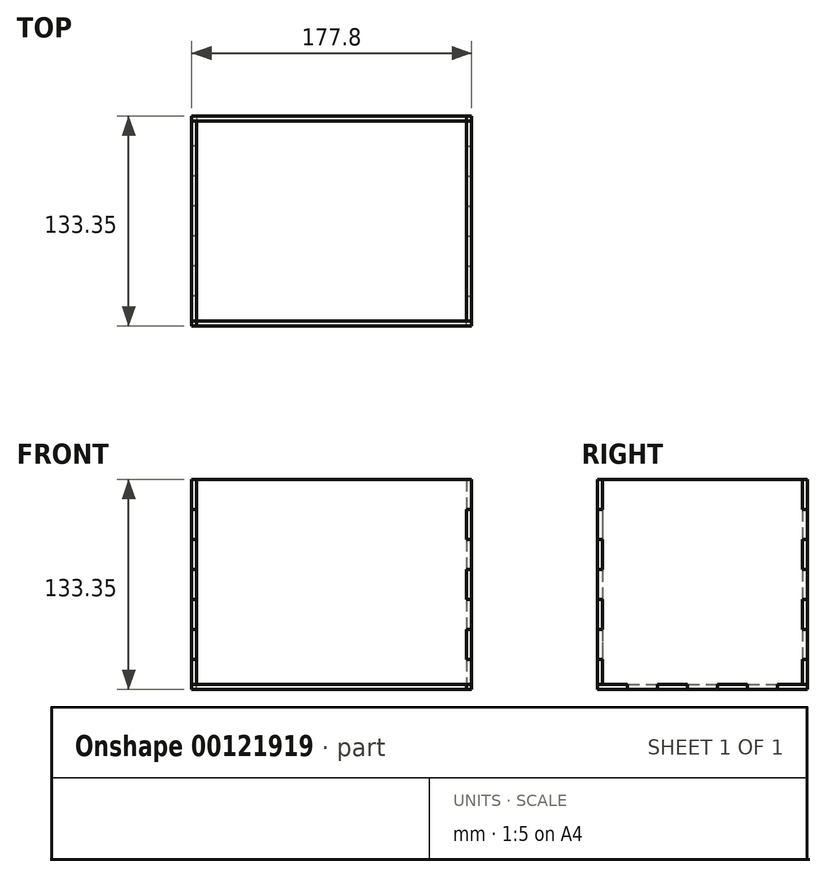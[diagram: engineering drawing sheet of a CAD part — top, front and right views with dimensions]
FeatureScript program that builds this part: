
annotation { "Feature Type Name" : "Feature", "Feature Type Description" : "" }
export const myFeature = defineFeature(function(context is Context, id is Id, definition is map)
    precondition{}
    {
        {
            var Q0;
            Q0=qCreatedBy(makeId("Top.planeOp"),FACE);
            var sketch = newSketch(context, id + "F0", { "sketchPlane" : qUnion([Q0])});
            skLineSegment(sketch, "E0.bottom", {"start": v(-88.9, 66.67) * mm, "end": v(88.9, 66.67) * mm});
            skLineSegment(sketch, "E0.top", {"start": v(-88.9, -66.68) * mm, "end": v(88.9, -66.68) * mm});
            skLineSegment(sketch, "E0.left", {"start": v(-88.9, 66.67) * mm, "end": v(-88.9, -66.68) * mm});
            skLineSegment(sketch, "E0.right", {"start": v(88.9, 66.68) * mm, "end": v(88.9, -66.68) * mm});
            skPoint(sketch, "E0.middle", {"position": v(0, 0) * mm});
            skSolve(sketch);
        }
        {
            var Q0;
            Q0=makeQuery(id+"F0.imprint","IMPRINT",FACE,{"disambiguationData":[TD([[makeQuery(id+"F0.imprint","IMPRINT",EDGE,{"derivedFrom":sQuery(id+"F0.wireOp",EDGE,"E0.bottom")}),-1.0]])]});
            extrude(context, id + "F1", {"entities" : qUnion([Q0]), "depth" : 3.17 * mm});
        }
        {
            var Q0;
            Q0=makeQuery(id+"F1.opExtrude","CAP_FACE",FACE,{"disambiguationData":[OSD([sQuery(id+"F0.wireOp",EDGE,"E0.bottom"),sQuery(id+"F0.wireOp",EDGE,"E0.top"),sQuery(id+"F0.wireOp",EDGE,"E0.left"),sQuery(id+"F0.wireOp",EDGE,"E0.right")])],"isStart":true});
            var sketch = newSketch(context, id + "F2", { "sketchPlane" : qUnion([Q0])});
            skLineSegment(sketch, "E1.bottom", {"start": v(88.9, 66.68) * mm, "end": v(85.72, 66.68) * mm});
            skLineSegment(sketch, "E1.top", {"start": v(88.9, -66.67) * mm, "end": v(85.73, -66.67) * mm});
            skLineSegment(sketch, "E1.left", {"start": v(88.9, 66.68) * mm, "end": v(88.9, -66.67) * mm});
            skLineSegment(sketch, "E1.right", {"start": v(85.73, 66.68) * mm, "end": v(85.73, -66.67) * mm});
            skSolve(sketch);
        }
        {
            var Q0;
            Q0 = qSketchRegion(id + "F2", true);
            extrude(context, id + "F3", {"entities" : qUnion([Q0]), "oppositeDirection" : true, "depth" : 133.35 * mm});
        }
        {
            var Q0;
            Q0=makeQuery(id+"F3.opExtrude","SWEPT_FACE",FACE,{"disambiguationData":[OSD([sQuery(id+"F2.wireOp",EDGE,"E1.left")])]});
            var sketch = newSketch(context, id + "F4", { "sketchPlane" : qUnion([Q0])});
            skLineSegment(sketch, "E2.bottom", {"start": v(-66.68, 0) * mm, "end": v(-47.63, 0) * mm});
            skLineSegment(sketch, "E2.top", {"start": v(-66.68, 3.18) * mm, "end": v(-47.63, 3.18) * mm});
            skLineSegment(sketch, "E2.left", {"start": v(-66.68, 0) * mm, "end": v(-66.68, 3.18) * mm});
            skLineSegment(sketch, "E2.right", {"start": v(-47.63, 0) * mm, "end": v(-47.63, 3.18) * mm});
            skLineSegment(sketch, "E3.1.0.0", {"start": v(-28.58, 0) * mm, "end": v(-28.58, 3.18) * mm});
            skLineSegment(sketch, "E3.1.0.1", {"start": v(-28.58, 3.18) * mm, "end": v(-9.53, 3.18) * mm});
            skLineSegment(sketch, "E3.1.0.2", {"start": v(-28.58, 0) * mm, "end": v(-9.53, 0) * mm});
            skLineSegment(sketch, "E3.1.0.3", {"start": v(-9.53, 0) * mm, "end": v(-9.53, 3.18) * mm});
            skLineSegment(sketch, "E3.2.0.0", {"start": v(9.52, 0) * mm, "end": v(9.52, 3.18) * mm});
            skLineSegment(sketch, "E3.2.0.1", {"start": v(9.52, 3.18) * mm, "end": v(28.57, 3.18) * mm});
            skLineSegment(sketch, "E3.2.0.2", {"start": v(9.52, 0) * mm, "end": v(28.57, 0) * mm});
            skLineSegment(sketch, "E3.2.0.3", {"start": v(28.57, 0) * mm, "end": v(28.57, 3.18) * mm});
            skLineSegment(sketch, "E3.3.0.0", {"start": v(47.62, 0) * mm, "end": v(47.62, 3.18) * mm});
            skLineSegment(sketch, "E3.3.0.1", {"start": v(47.62, 3.18) * mm, "end": v(66.67, 3.18) * mm});
            skLineSegment(sketch, "E3.3.0.2", {"start": v(47.62, 0) * mm, "end": v(66.67, 0) * mm});
            skLineSegment(sketch, "E3.3.0.3", {"start": v(66.67, 0) * mm, "end": v(66.67, 3.18) * mm});
            skLineSegment(sketch, "E3.direction1", {"start": v(-66.68, 0) * mm, "end": v(-28.58, 0) * mm, "construction": true});
            skSolve(sketch);
        }
        {
            var Q0;
            Q0 = qSketchRegion(id + "F4", true);
            extrude(context, id + "F5", {"entities" : qUnion([Q0]), "operationType" : NewBodyOperationType.REMOVE, "oppositeDirection" : true, "depth" : 3.17 * mm});
        }
        {
            var Q0;
            Q0=makeQuery(id+"F1.opExtrude","SWEPT_FACE",FACE,{"disambiguationData":[OSD([sQuery(id+"F0.wireOp",EDGE,"E0.bottom")])]});
            var sketch = newSketch(context, id + "F6", { "sketchPlane" : qUnion([Q0])});
            skLineSegment(sketch, "E4.bottom", {"start": v(88.9, 0) * mm, "end": v(-88.9, 0) * mm});
            skLineSegment(sketch, "E4.top", {"start": v(88.9, 133.35) * mm, "end": v(-88.9, 133.35) * mm});
            skLineSegment(sketch, "E4.left", {"start": v(88.9, 0) * mm, "end": v(88.9, 133.35) * mm});
            skLineSegment(sketch, "E4.right", {"start": v(-88.9, 0) * mm, "end": v(-88.9, 133.35) * mm});
            skSolve(sketch);
        }
        {
            var Q0;
            {var subQ0=sQuery(id+"F6.wireOp",EDGE,"E4.top");Q0=makeQuery(id+"F6.imprint","IMPRINT",FACE,{"disambiguationData":[TD([[makeQuery(id+"F6.imprint","IMPRINT",EDGE,{"derivedFrom":subQ0}),1.0]])]});}
            extrude(context, id + "F7", {"entities" : qUnion([Q0]), "oppositeDirection" : true, "depth" : 3.17 * mm});
        }
        {
            var Q0;
            Q0=makeQuery(id+"F3.opExtrude","SWEPT_FACE",FACE,{"disambiguationData":[OSD([sQuery(id+"F2.wireOp",EDGE,"E1.left")])]});
            var sketch = newSketch(context, id + "F8", { "sketchPlane" : qUnion([Q0])});
            skLineSegment(sketch, "E5.bottom", {"start": v(66.68, 133.35) * mm, "end": v(63.5, 133.35) * mm});
            skLineSegment(sketch, "E5.top", {"start": v(66.68, 114.3) * mm, "end": v(63.5, 114.3) * mm});
            skLineSegment(sketch, "E5.left", {"start": v(66.68, 133.35) * mm, "end": v(66.68, 114.3) * mm});
            skLineSegment(sketch, "E5.right", {"start": v(63.5, 133.35) * mm, "end": v(63.5, 114.3) * mm});
            skLineSegment(sketch, "E6.0.1.0", {"start": v(66.68, 95.25) * mm, "end": v(66.68, 76.2) * mm});
            skLineSegment(sketch, "E6.0.1.1", {"start": v(63.5, 95.25) * mm, "end": v(63.5, 76.2) * mm});
            skLineSegment(sketch, "E6.0.1.2", {"start": v(66.68, 95.25) * mm, "end": v(63.5, 95.25) * mm});
            skLineSegment(sketch, "E6.0.1.3", {"start": v(66.68, 76.2) * mm, "end": v(63.5, 76.2) * mm});
            skLineSegment(sketch, "E6.0.2.0", {"start": v(66.68, 57.15) * mm, "end": v(66.68, 38.1) * mm});
            skLineSegment(sketch, "E6.0.2.1", {"start": v(63.5, 57.15) * mm, "end": v(63.5, 38.1) * mm});
            skLineSegment(sketch, "E6.0.2.2", {"start": v(66.68, 57.15) * mm, "end": v(63.5, 57.15) * mm});
            skLineSegment(sketch, "E6.0.2.3", {"start": v(66.68, 38.1) * mm, "end": v(63.5, 38.1) * mm});
            skLineSegment(sketch, "E6.0.3.0", {"start": v(66.68, 19.05) * mm, "end": v(66.68, 0) * mm});
            skLineSegment(sketch, "E6.0.3.1", {"start": v(63.5, 19.05) * mm, "end": v(63.5, 0) * mm});
            skLineSegment(sketch, "E6.0.3.2", {"start": v(66.68, 19.05) * mm, "end": v(63.5, 19.05) * mm});
            skLineSegment(sketch, "E6.0.3.3", {"start": v(66.68, 0) * mm, "end": v(63.5, 0) * mm});
            skLineSegment(sketch, "E6.direction1", {"start": v(66.68, 114.3) * mm, "end": v(94.5, 114.3) * mm, "construction": true});
            skLineSegment(sketch, "E6.direction2", {"start": v(66.68, 114.3) * mm, "end": v(66.68, 76.2) * mm, "construction": true});
            skLineSegment(sketch, "E7.bottom", {"start": v(-66.68, 133.35) * mm, "end": v(-63.5, 133.35) * mm});
            skLineSegment(sketch, "E7.top", {"start": v(-66.68, 114.3) * mm, "end": v(-63.5, 114.3) * mm});
            skLineSegment(sketch, "E7.left", {"start": v(-66.68, 133.35) * mm, "end": v(-66.68, 114.3) * mm});
            skLineSegment(sketch, "E7.right", {"start": v(-63.5, 133.35) * mm, "end": v(-63.5, 114.3) * mm});
            skLineSegment(sketch, "E8.0.1.0", {"start": v(-66.68, 95.25) * mm, "end": v(-66.68, 76.2) * mm});
            skLineSegment(sketch, "E8.0.1.1", {"start": v(-63.5, 95.25) * mm, "end": v(-63.5, 76.2) * mm});
            skLineSegment(sketch, "E8.0.1.2", {"start": v(-66.68, 95.25) * mm, "end": v(-63.5, 95.25) * mm});
            skLineSegment(sketch, "E8.0.1.3", {"start": v(-66.68, 76.2) * mm, "end": v(-63.5, 76.2) * mm});
            skLineSegment(sketch, "E8.0.2.0", {"start": v(-66.68, 57.15) * mm, "end": v(-66.68, 38.1) * mm});
            skLineSegment(sketch, "E8.0.2.1", {"start": v(-63.5, 57.15) * mm, "end": v(-63.5, 38.1) * mm});
            skLineSegment(sketch, "E8.0.2.2", {"start": v(-66.68, 57.15) * mm, "end": v(-63.5, 57.15) * mm});
            skLineSegment(sketch, "E8.0.2.3", {"start": v(-66.68, 38.1) * mm, "end": v(-63.5, 38.1) * mm});
            skLineSegment(sketch, "E8.0.3.0", {"start": v(-66.68, 19.05) * mm, "end": v(-66.68, 0) * mm});
            skLineSegment(sketch, "E8.0.3.1", {"start": v(-63.5, 19.05) * mm, "end": v(-63.5, 0) * mm});
            skLineSegment(sketch, "E8.0.3.2", {"start": v(-66.68, 19.05) * mm, "end": v(-63.5, 19.05) * mm});
            skLineSegment(sketch, "E8.0.3.3", {"start": v(-66.68, 0) * mm, "end": v(-63.5, 0) * mm});
            skLineSegment(sketch, "E8.direction1", {"start": v(-66.68, 114.3) * mm, "end": v(-41.28, 114.3) * mm, "construction": true});
            skLineSegment(sketch, "E8.direction2", {"start": v(-66.68, 114.3) * mm, "end": v(-66.68, 76.2) * mm, "construction": true});
            skSolve(sketch);
        }
        {
            var Q0;
            Q0 = qSketchRegion(id + "F8", true);
            extrude(context, id + "F9", {"entities" : qUnion([Q0]), "operationType" : NewBodyOperationType.REMOVE, "oppositeDirection" : true, "depth" : 3.17 * mm});
        }
        {
            var Q0;
            Q0=qCreatedBy(makeId("Front.planeOp"),FACE);
            var sketch = newSketch(context, id + "F10", { "sketchPlane" : qUnion([Q0])});
            skLineSegment(sketch, "E9", {"start": v(0, 74.72) * mm, "end": v(0, 0) * mm});
            skSolve(sketch);
        }
        {
            var Q0;
            Q0=makeQuery(id+"F7.opExtrude","SWEPT_BODY",BODY,{"disambiguationData":[OSD([sQuery(id+"F0.wireOp",EDGE,"E0.bottom"),sQuery(id+"F6.wireOp",EDGE,"E4.top"),sQuery(id+"F6.wireOp",EDGE,"E4.left"),sQuery(id+"F6.wireOp",EDGE,"E4.right")])]});
            var Q1;
            Q1=makeQuery(id+"F3.opExtrude","SWEPT_BODY",BODY,{"disambiguationData":[OSD([sQuery(id+"F2.wireOp",EDGE,"E1.bottom"),sQuery(id+"F2.wireOp",EDGE,"E1.top"),sQuery(id+"F2.wireOp",EDGE,"E1.left"),sQuery(id+"F2.wireOp",EDGE,"E1.right")])]});
            var Q2;
            Q2=sQuery(id+"F10.wireOp",EDGE,"E9");
            circularPattern(context, id + "F11", {"entities" : qUnion([Q0, Q1]), "axis" : qUnion([Q2]), "angle" : 180 * degree, "instanceCount" : 2});
        }
        {
            var Q0;
            Q0=makeQuery(id+"F3.opExtrude","SWEPT_BODY",BODY,{"disambiguationData":[OSD([sQuery(id+"F2.wireOp",EDGE,"E1.bottom"),sQuery(id+"F2.wireOp",EDGE,"E1.top"),sQuery(id+"F2.wireOp",EDGE,"E1.left"),sQuery(id+"F2.wireOp",EDGE,"E1.right")])]});
            var Q1;
            Q1=makeQuery(id+"F11.opPattern","COPY",BODY,{"derivedFrom":makeQuery(id+"F3.opExtrude","SWEPT_BODY",BODY,{"disambiguationData":[OSD([sQuery(id+"F2.wireOp",EDGE,"E1.bottom"),sQuery(id+"F2.wireOp",EDGE,"E1.top"),sQuery(id+"F2.wireOp",EDGE,"E1.left"),sQuery(id+"F2.wireOp",EDGE,"E1.right")])]}),"instanceName":"1"});
            var Q2;
            Q2=makeQuery(id+"F1.opExtrude","SWEPT_BODY",BODY,{"disambiguationData":[OSD([sQuery(id+"F0.wireOp",EDGE,"E0.bottom"),sQuery(id+"F0.wireOp",EDGE,"E0.top"),sQuery(id+"F0.wireOp",EDGE,"E0.left"),sQuery(id+"F0.wireOp",EDGE,"E0.right")])]});
            var Q3;
            Q3=makeQuery(id+"F7.opExtrude","SWEPT_BODY",BODY,{"disambiguationData":[OSD([sQuery(id+"F0.wireOp",EDGE,"E0.bottom"),sQuery(id+"F6.wireOp",EDGE,"E4.top"),sQuery(id+"F6.wireOp",EDGE,"E4.left"),sQuery(id+"F6.wireOp",EDGE,"E4.right")])]});
            var Q4;
            Q4=makeQuery(id+"F11.opPattern","COPY",BODY,{"derivedFrom":makeQuery(id+"F7.opExtrude","SWEPT_BODY",BODY,{"disambiguationData":[OSD([sQuery(id+"F0.wireOp",EDGE,"E0.bottom"),sQuery(id+"F6.wireOp",EDGE,"E4.top"),sQuery(id+"F6.wireOp",EDGE,"E4.left"),sQuery(id+"F6.wireOp",EDGE,"E4.right")])]}),"instanceName":"1"});
            booleanBodies(context, id + "F12", {"operationType" : BooleanOperationType.SUBTRACTION, "tools" : qUnion([Q0, Q1]), "targets" : qUnion([Q2, Q3, Q4]), "keepTools" : true});
        }
    });
